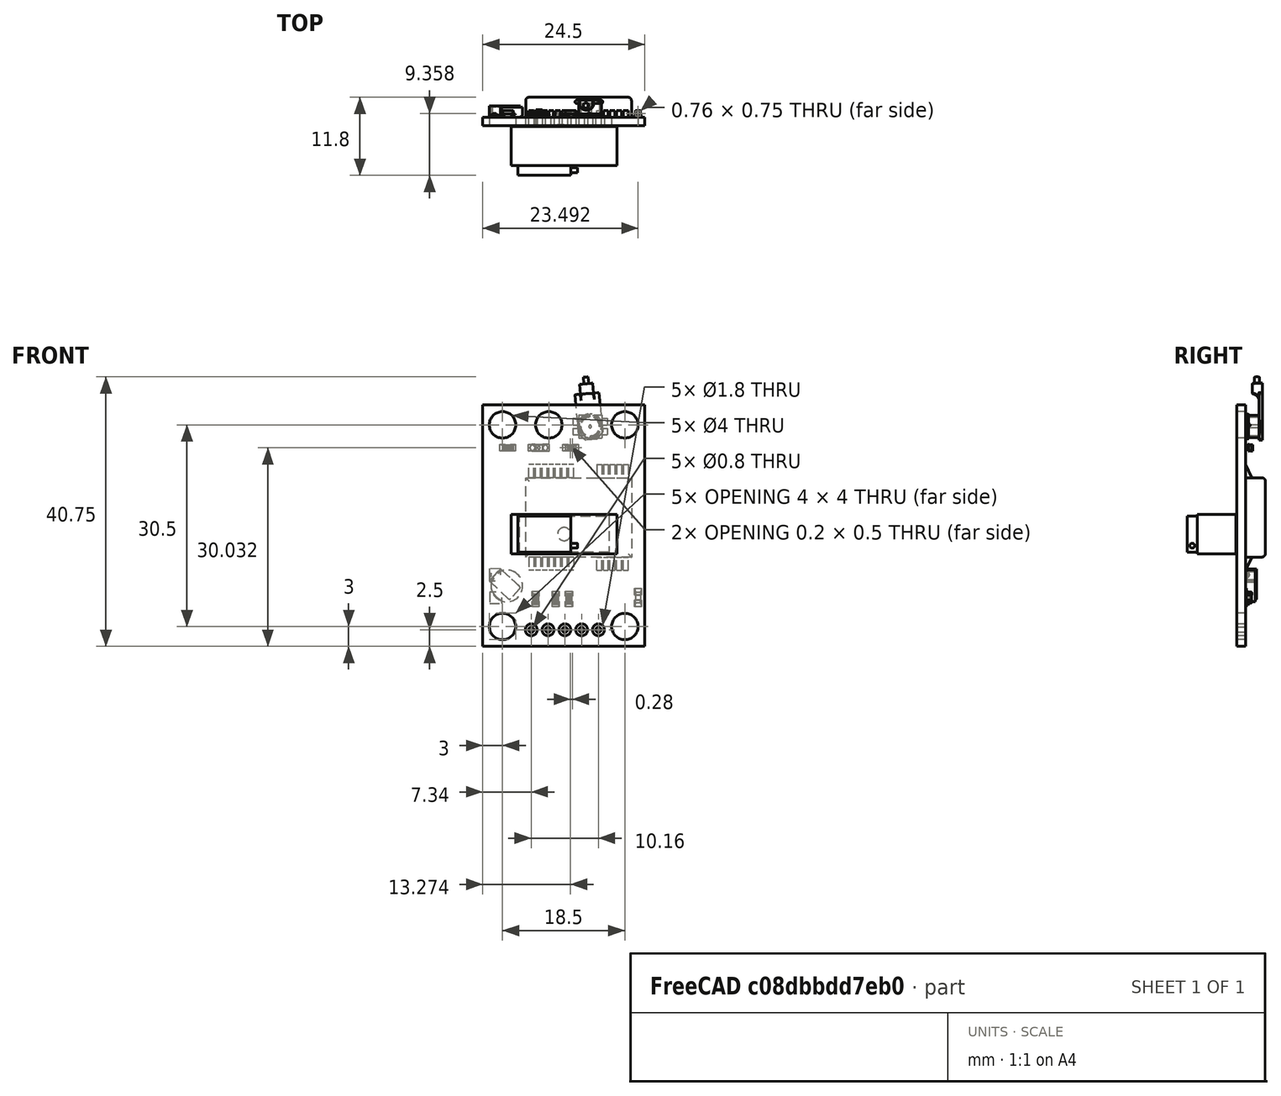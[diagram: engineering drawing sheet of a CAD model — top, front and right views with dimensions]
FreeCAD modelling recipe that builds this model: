
FCSTD DOCUMENT  (FreeCAD 0.18.3R)
Label: neo6mv2
License: All rights reserved
LicenseURL: http://en.wikipedia.org/wiki/All_rights_reserved
objects: Part::Cylinder×20, Part::Feature×12, Part::Cut×6, Part::MultiFuse×2, Part::Box×2, App::Part×1, Part::Fillet×1
note: 43 computed .brp shape members not serialized (recipe doc carries the construction recipe); baked Part::Feature solids carry a one-line shape summary decoded from their .brp

FEATURE [Part::Feature] Part__Feature  label="GPS_pcb"
  Placement = pos=(-12.25,0,-1.25) rot=(0,0,1;0rad)
  shape: bbox 24.5 x 4.3 x 36.5 mm, 145 faces, 25 solids (baked)
FEATURE [Part::Feature] Part__Feature001  label="GPS_cap"
  Placement = pos=(-1.008,1.35775,-12.1193) rot=(0,-1,0;1.5708rad)
  shape: bbox 1.226 x 0.955 x 3.329 mm, 56 faces (baked)
FEATURE [Part::Feature] Part__Feature002  label="GPS_res221"
  Placement = pos=(-13.49,1.3,-12.319) rot=(0,-1,0;1.5708rad)
  shape: bbox 1.02 x 0.6154 x 2.362 mm, 138 faces, 4 solids (baked)
FEATURE [Part::Feature] Part__Feature003  label="GPS_res472"
  Placement = pos=(-11.4616,1.3,-12.319) rot=(0,1,0;1.5708rad)
  shape: bbox 1.02 x 0.6154 x 2.362 mm, 124 faces, 4 solids (baked)
FEATURE [Part::Feature] Part__Feature004  label="GPS_res473"
  Placement = pos=(-16.49,1.3,-12.319) rot=(0,-1,0;1.5708rad)
  shape: bbox 1.02 x 0.6154 x 2.362 mm, 138 faces, 4 solids (baked)
FEATURE [Part::Feature] Part__Feature005  label="GPS_battery"
  Placement = pos=(-14.7943,1.29979,13.0331) rot=(-0.850961,-0.371393,-0.371393;1.73149rad)
  shape: bbox 5.675 x 1.701 x 5.675 mm, 36 faces (baked)
FEATURE [Part::Feature] Part__Feature006  label="GPS_res474"
  Placement = pos=(-20.7044,1.68325,10.5205) rot=(0,0,1;0rad)
  shape: bbox 2.362 x 0.6154 x 1.02 mm, 124 faces, 4 solids (baked)
FEATURE [Part::Feature] Part__Feature007  label="GPS_res100"
  Placement = pos=(-11.2066,1.68325,10.5205) rot=(0,0,1;0rad)
  shape: bbox 2.362 x 0.6154 x 1.02 mm, 124 faces, 4 solids (baked)
FEATURE [Part::Feature] Part__Feature008  label="GPS_led"
  Placement = pos=(-15.9936,1.65117,10.5305) rot=(0,0,1;0rad)
  shape: bbox 3.551 x 0.7528 x 1.711 mm, 57 faces, 2 solids (baked)
FEATURE [Part::Feature] Part__Feature009  label="GPS_connector"
  Placement = pos=(-0.2977,1.3,-0.303869) rot=(-1,0,0;1.5708rad)
  shape: bbox 5.25 x 2.059 x 3.5 mm, 38 faces (baked)
FEATURE [Part::Feature] Part__Feature010  label="Antenna_connector"
  Placement = pos=(1.97581,1.55,13.0153) rot=(-0.997842,-0.046433,-0.046433;1.57296rad)
  shape: bbox 4.331 x 2.3 x 9.572 mm, 71 faces (baked)
FEATURE [Part::Feature] Part__Feature011  label="Antenna"
  Placement = pos=(-16,-5,5) rot=(0.57735,0.57735,0.57735;4.18879rad)
  shape: bbox 16.04 x 7.828 x 6.038 mm, 26 faces (baked)
FEATURE [App::Part] ublox_NEO_6M  label="ublox NEO-6M"
  Group = -> [Part__Feature,Part__Feature001,Part__Feature002,Part__Feature003,Part__Feature004,Part__Feature005,Part__Feature006,Part__Feature007,Part__Feature008,Part__Feature009,Part__Feature010,Part__Feature011]
  Origin = -> Origin
FEATURE [Part::Cylinder] Cylinder153
  Angle = 360
  AttacherType = Attacher::AttachEngine3D
  Height = 1.3
  Radius = 0.9
FEATURE [Part::Cylinder] Cylinder162
  Angle = 360
  AttacherType = Attacher::AttachEngine3D
  Height = 1.3
  Radius = 0.4
FEATURE [Part::Cut] Cut115  label="contact"
  Base = -> Cylinder153
  Placement = pos=(-7,1.3,-17) rot=(1,0,0;1.5708rad)
  Tool = -> Cylinder162
FEATURE [Part::Cylinder] Cylinder163 .. Cylinder167  x5 (patterned run collapsed; names and placements below)
  Angle = 360
  AttacherType = Attacher::AttachEngine3D
  Height = 1.3
  Radius = 0.9
  placements: 5 in arithmetic series — first pos=(-7,1.3,-17) rot=(1,0,0;1.5708rad), step (-2.54,0,0), last pos=(-17.16,1.3,-17) rot=(1,0,0;1.5708rad)
FEATURE [Part::MultiFuse] Fusion
  Shapes = -> [Cylinder163,Cylinder166,Cylinder165,Cylinder167,Cylinder164]
FEATURE [Part::Box] Box  label="Cube"
  AttacherType = Attacher::AttachEngine3D
  Height = 36.5
  Length = 24.5
  Placement = pos=(-24.5,0,-19.5) rot=(0,0,1;0rad)
  Width = 1.3
FEATURE [Part::Cylinder] Cylinder
  Angle = 360
  AttacherType = Attacher::AttachEngine3D
  Height = 10
  Placement = pos=(-3,2,14) rot=(1,0,0;1.5708rad)
  Radius = 2
FEATURE [Part::Cylinder] Cylinder168
  Angle = 360
  AttacherType = Attacher::AttachEngine3D
  Height = 10
  Placement = pos=(-14.5,2,14) rot=(1,0,0;1.5708rad)
  Radius = 2
FEATURE [Part::Cylinder] Cylinder169
  Angle = 360
  AttacherType = Attacher::AttachEngine3D
  Height = 10
  Placement = pos=(-21.5,2,14) rot=(1,0,0;1.5708rad)
  Radius = 2
FEATURE [Part::Cylinder] Cylinder170
  Angle = 360
  AttacherType = Attacher::AttachEngine3D
  Height = 10
  Placement = pos=(-3,2,-16.5) rot=(1,0,0;1.5708rad)
  Radius = 2
FEATURE [Part::Cylinder] Cylinder171
  Angle = 360
  AttacherType = Attacher::AttachEngine3D
  Height = 10
  Placement = pos=(-21.5,2,-16.5) rot=(1,0,0;1.5708rad)
  Radius = 2
FEATURE [Part::MultiFuse] Fusion001  label="pcb cutouts"
  Shapes = -> [Fusion,Cylinder,Cylinder168,Cylinder169,Cylinder170,Cylinder171]
FEATURE [Part::Cut] Cut  label="PCB"
  Base = -> Box
  Tool = -> Fusion001
FEATURE [Part::Box] Box001  label="Cube001"
  AttacherType = Attacher::AttachEngine3D
  Height = 12
  Length = 16
  Placement = pos=(-18,1.3,-6) rot=(0,0,1;0rad)
  Width = 3
FEATURE [Part::Fillet] Fillet  label="neo6m chip"
  Base = -> Box001
  Edges = 4 edges r=0.5: [Edge3,Edge7,Edge11,Edge12]
FEATURE [Part::Cylinder] Cylinder172
  Angle = 360
  AttacherType = Attacher::AttachEngine3D
  Height = 1.3
  Radius = 0.4
FEATURE [Part::Cylinder] Cylinder173
  Angle = 360
  AttacherType = Attacher::AttachEngine3D
  Height = 1.3
  Radius = 0.9
FEATURE [Part::Cut] Cut116  label="contact001"
  Base = -> Cylinder173
  Placement = pos=(-9.54,1.3,-17) rot=(1,0,0;1.5708rad)
  Tool = -> Cylinder172
FEATURE [Part::Cylinder] Cylinder174
  Angle = 360
  AttacherType = Attacher::AttachEngine3D
  Height = 1.3
  Radius = 0.4
FEATURE [Part::Cylinder] Cylinder175
  Angle = 360
  AttacherType = Attacher::AttachEngine3D
  Height = 1.3
  Radius = 0.9
FEATURE [Part::Cut] Cut117  label="contact002"
  Base = -> Cylinder175
  Placement = pos=(-12.08,1.3,-17) rot=(1,0,0;1.5708rad)
  Tool = -> Cylinder174
FEATURE [Part::Cylinder] Cylinder176
  Angle = 360
  AttacherType = Attacher::AttachEngine3D
  Height = 1.3
  Radius = 0.4
FEATURE [Part::Cylinder] Cylinder177
  Angle = 360
  AttacherType = Attacher::AttachEngine3D
  Height = 1.3
  Radius = 0.9
FEATURE [Part::Cut] Cut118  label="contact003"
  Base = -> Cylinder177
  Placement = pos=(-14.62,1.3,-17) rot=(1,0,0;1.5708rad)
  Tool = -> Cylinder176
FEATURE [Part::Cylinder] Cylinder178
  Angle = 360
  AttacherType = Attacher::AttachEngine3D
  Height = 1.3
  Radius = 0.4
FEATURE [Part::Cylinder] Cylinder179
  Angle = 360
  AttacherType = Attacher::AttachEngine3D
  Height = 1.3
  Radius = 0.9
FEATURE [Part::Cut] Cut119  label="contact004"
  Base = -> Cylinder179
  Placement = pos=(-17.16,1.3,-17) rot=(1,0,0;1.5708rad)
  Tool = -> Cylinder178
